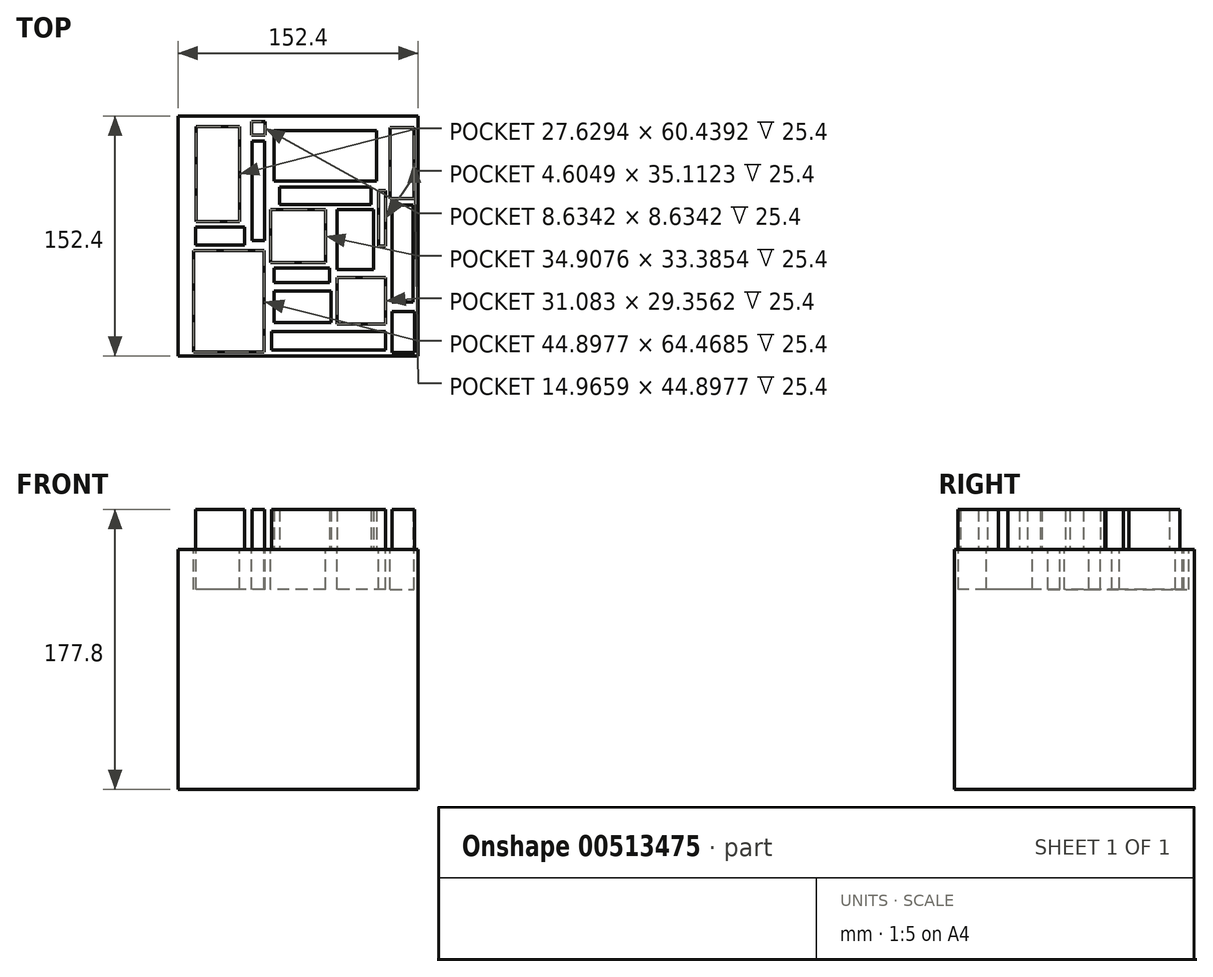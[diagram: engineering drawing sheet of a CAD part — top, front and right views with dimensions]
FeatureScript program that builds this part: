
annotation { "Feature Type Name" : "Feature", "Feature Type Description" : "" }
export const myFeature = defineFeature(function(context is Context, id is Id, definition is map)
    precondition{}
    {
        {
            var Q0;
            Q0=qCreatedBy(makeId("Top.planeOp"),FACE);
            var sketch = newSketch(context, id + "F0", { "sketchPlane" : qUnion([Q0])});
            skLineSegment(sketch, "E0.bottom", {"start": v(76.2, -76.2) * mm, "end": v(-76.2, -76.2) * mm});
            skLineSegment(sketch, "E0.top", {"start": v(76.2, 76.2) * mm, "end": v(-76.2, 76.2) * mm});
            skLineSegment(sketch, "E0.left", {"start": v(76.2, -76.2) * mm, "end": v(76.2, 76.2) * mm});
            skLineSegment(sketch, "E0.right", {"start": v(-76.2, -76.2) * mm, "end": v(-76.2, 76.2) * mm});
            skPoint(sketch, "E0.middle", {"position": v(0, 0) * mm});
            skSolve(sketch);
        }
        {
            var Q0;
            Q0=makeQuery(id+"F0.imprint","IMPRINT",FACE,{"disambiguationData":[TD([[makeQuery(id+"F0.imprint","IMPRINT",EDGE,{"derivedFrom":sQuery(id+"F0.wireOp",EDGE,"E0.bottom")}),-1.0]])]});
            extrude(context, id + "F1", {"entities" : qUnion([Q0]), "depth" : 152.4 * mm});
        }
        {
            var Q0;
            Q0=makeQuery(id+"F1.opExtrude","CAP_FACE",FACE,{"disambiguationData":[OSD([sQuery(id+"F0.wireOp",EDGE,"E0.bottom"),sQuery(id+"F0.wireOp",EDGE,"E0.top"),sQuery(id+"F0.wireOp",EDGE,"E0.left"),sQuery(id+"F0.wireOp",EDGE,"E0.right")])],"isStart":false});
            var sketch = newSketch(context, id + "F2", { "sketchPlane" : qUnion([Q0])});
            skLineSegment(sketch, "E1.bottom", {"start": v(17.45, -16.7) * mm, "end": v(-17.45, -16.7) * mm});
            skLineSegment(sketch, "E1.top", {"start": v(17.45, 16.7) * mm, "end": v(-17.45, 16.7) * mm});
            skLineSegment(sketch, "E1.left", {"start": v(17.45, -16.7) * mm, "end": v(17.45, 16.7) * mm});
            skLineSegment(sketch, "E1.right", {"start": v(-17.45, -16.7) * mm, "end": v(-17.45, 16.7) * mm});
            skPoint(sketch, "E1.middle", {"position": v(0, 0) * mm});
            skLineSegment(sketch, "E2.bottom", {"start": v(20.04, -29.64) * mm, "end": v(-15.07, -29.64) * mm});
            skLineSegment(sketch, "E2.top", {"start": v(20.04, -20.43) * mm, "end": v(-15.07, -20.43) * mm});
            skLineSegment(sketch, "E2.left", {"start": v(20.04, -29.64) * mm, "end": v(20.04, -20.43) * mm});
            skLineSegment(sketch, "E2.right", {"start": v(-15.07, -29.64) * mm, "end": v(-15.07, -20.43) * mm});
            skPoint(sketch, "E2.middle", {"position": v(2.49, -25.04) * mm});
            skLineSegment(sketch, "E3.bottom", {"start": v(-11.61, 31.08) * mm, "end": v(46.52, 31.08) * mm});
            skLineSegment(sketch, "E3.top", {"start": v(-11.61, 20.15) * mm, "end": v(46.52, 20.15) * mm});
            skLineSegment(sketch, "E3.left", {"start": v(-11.61, 31.08) * mm, "end": v(-11.61, 20.15) * mm});
            skLineSegment(sketch, "E3.right", {"start": v(46.52, 31.08) * mm, "end": v(46.52, 20.15) * mm});
            skPoint(sketch, "E3.middle", {"position": v(17.45, 25.61) * mm});
            skLineSegment(sketch, "E4.bottom", {"start": v(-29.17, -2.88) * mm, "end": v(-21.11, -2.88) * mm});
            skLineSegment(sketch, "E4.top", {"start": v(-29.17, 60.44) * mm, "end": v(-21.11, 60.44) * mm});
            skLineSegment(sketch, "E4.left", {"start": v(-29.17, -2.88) * mm, "end": v(-29.17, 60.44) * mm});
            skLineSegment(sketch, "E4.right", {"start": v(-21.11, -2.88) * mm, "end": v(-21.11, 60.44) * mm});
            skPoint(sketch, "E4.middle", {"position": v(-25.14, 28.78) * mm});
            skLineSegment(sketch, "E5.bottom", {"start": v(-21.4, -9.2) * mm, "end": v(-66.3, -9.2) * mm});
            skLineSegment(sketch, "E5.top", {"start": v(-21.4, -73.68) * mm, "end": v(-66.3, -73.68) * mm});
            skLineSegment(sketch, "E5.left", {"start": v(-21.4, -9.2) * mm, "end": v(-21.4, -73.68) * mm});
            skLineSegment(sketch, "E5.right", {"start": v(-66.3, -9.2) * mm, "end": v(-66.3, -73.68) * mm});
            skPoint(sketch, "E5.middle", {"position": v(-43.85, -41.44) * mm});
            skLineSegment(sketch, "E6.bottom", {"start": v(-37.23, 9.2) * mm, "end": v(-64.86, 9.2) * mm});
            skLineSegment(sketch, "E6.top", {"start": v(-37.23, 69.65) * mm, "end": v(-64.86, 69.65) * mm});
            skLineSegment(sketch, "E6.left", {"start": v(-37.23, 9.2) * mm, "end": v(-37.23, 69.65) * mm});
            skLineSegment(sketch, "E6.right", {"start": v(-64.86, 9.2) * mm, "end": v(-64.86, 69.65) * mm});
            skPoint(sketch, "E6.middle", {"position": v(-51.04, 39.43) * mm});
            skLineSegment(sketch, "E7.bottom", {"start": v(-34.06, 5.76) * mm, "end": v(-65.15, 5.76) * mm});
            skLineSegment(sketch, "E7.top", {"start": v(-34.06, -5.76) * mm, "end": v(-65.15, -5.76) * mm});
            skLineSegment(sketch, "E7.left", {"start": v(-34.06, 5.76) * mm, "end": v(-34.06, -5.76) * mm});
            skLineSegment(sketch, "E7.right", {"start": v(-65.15, 5.76) * mm, "end": v(-65.15, -5.76) * mm});
            skPoint(sketch, "E7.middle", {"position": v(-49.6, 0) * mm});
            skLineSegment(sketch, "E8.bottom", {"start": v(-15.07, 34.82) * mm, "end": v(49.98, 34.82) * mm});
            skLineSegment(sketch, "E8.top", {"start": v(-15.07, 67.06) * mm, "end": v(49.98, 67.06) * mm});
            skLineSegment(sketch, "E8.left", {"start": v(-15.07, 34.82) * mm, "end": v(-15.07, 67.06) * mm});
            skLineSegment(sketch, "E8.right", {"start": v(49.98, 34.82) * mm, "end": v(49.98, 67.06) * mm});
            skPoint(sketch, "E8.middle", {"position": v(17.45, 50.94) * mm});
            skLineSegment(sketch, "E9.bottom", {"start": v(-20.82, 64.18) * mm, "end": v(-29.46, 64.18) * mm});
            skLineSegment(sketch, "E9.top", {"start": v(-20.82, 72.81) * mm, "end": v(-29.46, 72.81) * mm});
            skLineSegment(sketch, "E9.left", {"start": v(-20.82, 64.18) * mm, "end": v(-20.82, 72.81) * mm});
            skLineSegment(sketch, "E9.right", {"start": v(-29.46, 64.18) * mm, "end": v(-29.46, 72.81) * mm});
            skPoint(sketch, "E9.middle", {"position": v(-25.14, 68.5) * mm});
            skLineSegment(sketch, "E10.bottom", {"start": v(58.6, 68.79) * mm, "end": v(73.58, 68.79) * mm});
            skLineSegment(sketch, "E10.top", {"start": v(58.6, 23.89) * mm, "end": v(73.58, 23.89) * mm});
            skLineSegment(sketch, "E10.left", {"start": v(58.6, 68.79) * mm, "end": v(58.6, 23.89) * mm});
            skLineSegment(sketch, "E10.right", {"start": v(73.58, 68.79) * mm, "end": v(73.58, 23.89) * mm});
            skPoint(sketch, "E10.middle", {"position": v(66.1, 46.34) * mm});
            skLineSegment(sketch, "E11.bottom", {"start": v(55.73, 28.78) * mm, "end": v(51.13, 28.78) * mm});
            skLineSegment(sketch, "E11.top", {"start": v(55.73, -6.33) * mm, "end": v(51.13, -6.33) * mm});
            skLineSegment(sketch, "E11.left", {"start": v(55.73, 28.78) * mm, "end": v(55.73, -6.33) * mm});
            skLineSegment(sketch, "E11.right", {"start": v(51.13, 28.78) * mm, "end": v(51.13, -6.33) * mm});
            skPoint(sketch, "E11.middle", {"position": v(53.43, 11.22) * mm});
            skLineSegment(sketch, "E12.bottom", {"start": v(47.96, 16.7) * mm, "end": v(24.94, 16.7) * mm});
            skLineSegment(sketch, "E12.top", {"start": v(47.96, -21.3) * mm, "end": v(24.94, -21.3) * mm});
            skLineSegment(sketch, "E12.left", {"start": v(47.96, 16.7) * mm, "end": v(47.96, -21.3) * mm});
            skLineSegment(sketch, "E12.right", {"start": v(24.94, 16.7) * mm, "end": v(24.94, -21.3) * mm});
            skPoint(sketch, "E12.middle", {"position": v(36.45, -2.3) * mm});
            skLineSegment(sketch, "E13.bottom", {"start": v(73, 19.57) * mm, "end": v(59.76, 19.57) * mm});
            skLineSegment(sketch, "E13.top", {"start": v(73, -42.02) * mm, "end": v(59.76, -42.02) * mm});
            skLineSegment(sketch, "E13.left", {"start": v(73, 19.57) * mm, "end": v(73, -42.02) * mm});
            skLineSegment(sketch, "E13.right", {"start": v(59.76, 19.57) * mm, "end": v(59.76, -42.02) * mm});
            skPoint(sketch, "E13.middle", {"position": v(66.38, -11.22) * mm});
            skLineSegment(sketch, "E14.bottom", {"start": v(55.73, -26.48) * mm, "end": v(24.65, -26.48) * mm});
            skLineSegment(sketch, "E14.top", {"start": v(55.73, -55.83) * mm, "end": v(24.65, -55.83) * mm});
            skLineSegment(sketch, "E14.left", {"start": v(55.73, -26.48) * mm, "end": v(55.73, -55.83) * mm});
            skLineSegment(sketch, "E14.right", {"start": v(24.65, -26.48) * mm, "end": v(24.65, -55.83) * mm});
            skPoint(sketch, "E14.middle", {"position": v(40.2, -41.16) * mm});
            skLineSegment(sketch, "E15.bottom", {"start": v(59.76, -48.06) * mm, "end": v(74.15, -48.06) * mm});
            skLineSegment(sketch, "E15.top", {"start": v(59.76, -73.97) * mm, "end": v(74.15, -73.97) * mm});
            skLineSegment(sketch, "E15.left", {"start": v(59.76, -48.06) * mm, "end": v(59.76, -73.97) * mm});
            skLineSegment(sketch, "E15.right", {"start": v(74.15, -48.06) * mm, "end": v(74.15, -73.97) * mm});
            skPoint(sketch, "E15.middle", {"position": v(66.96, -61.01) * mm});
            skLineSegment(sketch, "E16.bottom", {"start": v(55.73, -72.24) * mm, "end": v(-16.8, -72.24) * mm});
            skLineSegment(sketch, "E16.top", {"start": v(55.73, -60.73) * mm, "end": v(-16.8, -60.73) * mm});
            skLineSegment(sketch, "E16.left", {"start": v(55.73, -72.24) * mm, "end": v(55.73, -60.73) * mm});
            skLineSegment(sketch, "E16.right", {"start": v(-16.8, -72.24) * mm, "end": v(-16.8, -60.73) * mm});
            skPoint(sketch, "E16.middle", {"position": v(19.47, -66.48) * mm});
            skLineSegment(sketch, "E17.bottom", {"start": v(20.9, -34.82) * mm, "end": v(-15.36, -34.82) * mm});
            skLineSegment(sketch, "E17.top", {"start": v(20.9, -54.97) * mm, "end": v(-15.36, -54.97) * mm});
            skLineSegment(sketch, "E17.left", {"start": v(20.9, -34.82) * mm, "end": v(20.9, -54.97) * mm});
            skLineSegment(sketch, "E17.right", {"start": v(-15.36, -34.82) * mm, "end": v(-15.36, -54.97) * mm});
            skPoint(sketch, "E17.middle", {"position": v(2.78, -44.9) * mm});
            skSolve(sketch);
        }
        {
            var Q0;
            Q0 = qSketchRegion(id + "F2", true);
            extrude(context, id + "F3", {"entities" : qUnion([Q0]), "operationType" : NewBodyOperationType.ADD, "depth" : 25.4 * mm});
        }
        {
            var Q0;
            Q0=makeQuery(id+"F3.opExtrude","CAP_FACE",FACE,{"disambiguationData":[OSD([sQuery(id+"F2.wireOp",EDGE,"E6.bottom"),sQuery(id+"F2.wireOp",EDGE,"E6.top"),sQuery(id+"F2.wireOp",EDGE,"E6.left"),sQuery(id+"F2.wireOp",EDGE,"E6.right")])],"isStart":false});
            var Q1;
            Q1=makeQuery(id+"F3.opExtrude","CAP_FACE",FACE,{"disambiguationData":[OSD([sQuery(id+"F2.wireOp",EDGE,"E1.bottom"),sQuery(id+"F2.wireOp",EDGE,"E1.top"),sQuery(id+"F2.wireOp",EDGE,"E1.left"),sQuery(id+"F2.wireOp",EDGE,"E1.right")])],"isStart":false});
            var Q2;
            Q2=makeQuery(id+"F3.opExtrude","CAP_FACE",FACE,{"disambiguationData":[OSD([sQuery(id+"F2.wireOp",EDGE,"E14.bottom"),sQuery(id+"F2.wireOp",EDGE,"E14.top"),sQuery(id+"F2.wireOp",EDGE,"E14.left"),sQuery(id+"F2.wireOp",EDGE,"E14.right")])],"isStart":false});
            var Q3;
            Q3=makeQuery(id+"F3.opExtrude","CAP_FACE",FACE,{"disambiguationData":[OSD([sQuery(id+"F2.wireOp",EDGE,"E5.bottom"),sQuery(id+"F2.wireOp",EDGE,"E5.top"),sQuery(id+"F2.wireOp",EDGE,"E5.left"),sQuery(id+"F2.wireOp",EDGE,"E5.right")])],"isStart":false});
            var Q4;
            Q4=makeQuery(id+"F3.opExtrude","CAP_FACE",FACE,{"disambiguationData":[OSD([sQuery(id+"F2.wireOp",EDGE,"E10.bottom"),sQuery(id+"F2.wireOp",EDGE,"E10.top"),sQuery(id+"F2.wireOp",EDGE,"E10.left"),sQuery(id+"F2.wireOp",EDGE,"E10.right")])],"isStart":false});
            var Q5;
            Q5=makeQuery(id+"F3.opExtrude","CAP_FACE",FACE,{"disambiguationData":[OSD([sQuery(id+"F2.wireOp",EDGE,"E9.bottom"),sQuery(id+"F2.wireOp",EDGE,"E9.top"),sQuery(id+"F2.wireOp",EDGE,"E9.left"),sQuery(id+"F2.wireOp",EDGE,"E9.right")])],"isStart":false});
            var Q6;
            Q6=makeQuery(id+"F3.opExtrude","CAP_FACE",FACE,{"disambiguationData":[OSD([sQuery(id+"F2.wireOp",EDGE,"E11.bottom"),sQuery(id+"F2.wireOp",EDGE,"E11.top"),sQuery(id+"F2.wireOp",EDGE,"E11.left"),sQuery(id+"F2.wireOp",EDGE,"E11.right")])],"isStart":false});
            extrude(context, id + "F4", {"entities" : qUnion([Q0, Q1, Q2, Q3, Q4, Q5, Q6]), "operationType" : NewBodyOperationType.REMOVE, "oppositeDirection" : true, "depth" : 50.8 * mm});
        }
    });
